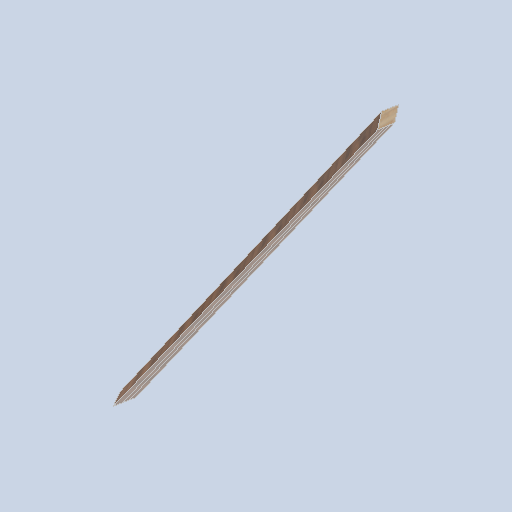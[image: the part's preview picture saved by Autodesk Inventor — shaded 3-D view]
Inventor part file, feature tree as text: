
AUTODESK INVENTOR PART (.ipt)
format: ipt  version: 2024.2 (Build 282272000, 272)  size: 129,536 bytes
history: native  units: in
note: dims shown in document units (in); Inventor stores cm internally (conversion verified against a paired STEP export)
features: sketch x4, other x3, plane x2
ambient origin geometry x8: Origin, YZ Plane, XZ Plane, XY Plane, X Axis, Y Axis, Z Axis, Center Point
bodies: Solid1 (feature_tree)
feature tree (9):
  other  "side_curve_beam_03_MIR.ipt"
  other  "Solid1::side_curve_beam_03_MIR.ipt"
  other  "TaggingFeature1"
  sketch  "Sketch1"  dims[d0=0.3937in]
  sketch  "Sketch2"
  sketch  "Sketch3"
  sketch  "Sketch4"
  plane  "Work Plane1"
  plane  "Work Plane2"
